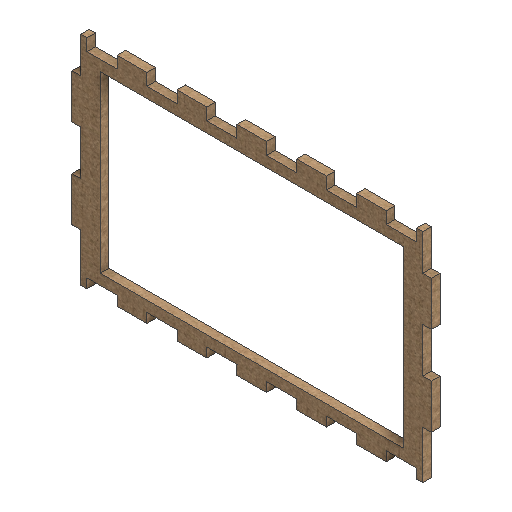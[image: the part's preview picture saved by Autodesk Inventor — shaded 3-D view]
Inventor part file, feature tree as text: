
AUTODESK INVENTOR PART (.ipt)
format: ipt  version: 2025.2 (Build 292293000, 293)  size: 389,120 bytes
history: native  units: mm
features: sketch x9, extrude x8, projected_geometry x3, mirror x1
ambient origin geometry x8: Origin, YZ Plane, XZ Plane, XY Plane, X Axis, Y Axis, Z Axis, Center Point
bodies: Solid1 (feature_tree)
feature tree (21):
  extrude  "Extrusion1"  Depth=102.0mm
  extrude  "Extrusion2"  Depth=210.0mm
  mirror  "Mirror1"
  extrude  "Extrusion3"  Depth=5.0mm
  extrude  "Extrusion4"  Depth=5.0mm TaperAngle=0.0deg
  extrude  "Extrusion5"  Depth=130.0mm
  extrude  "Extrusion7"  Depth=26.1mm
  extrude  "Extrusion8"  Depth=5.1mm TaperAngle=0.0deg
  extrude  "Extrusion9"  Depth=210.0mm
  sketch  "Sketch1"  dims[d0=177.0mm d1=102.0mm]
  sketch  "Sketch2"  dims[d2=130.0mm d3=210.0mm]
  sketch  "Sketch3"  dims[d7=100.0mm d8=5.0mm d9=0.0mm]
  sketch  "Sketch4"  dims[d10=20.0mm d13=130.0mm]
  projected_geometry  "Projected Loop1"
  sketch  "Sketch5"  dims[d14=26.05mm d15=26.1mm]
  projected_geometry  "Projected Loop2"
  sketch  "Sketch7"  dims[d16=5.1mm d17=10.0mm d18=0.0mm]
  sketch  "Sketch Rectangular Pattern2"  dims[d4=5.0mm d5=0.0mm d6=10.0mm]
  sketch  "Sketch8"  dims[d19=2.0mm d20=0.0mm d21=210.0mm]
  projected_geometry  "Projected Loop4"
  sketch  "Sketch9"  dims[d22=17.45mm d23=17.6mm d24=5.6mm d27=35.0mm d32=0.0mm d33=0.0mm d38=30.0mm d40=10.0mm d41=17.45mm d42=17.6mm d44=35.0mm d45=10.0mm d46=210.0mm d47=12.0mm d48=10.0mm d49=0.0mm d51=2.0mm d52=0.0mm d53=5.0mm d54=177.0mm d55=102.0mm d56=5.0mm d57=0.0mm]
